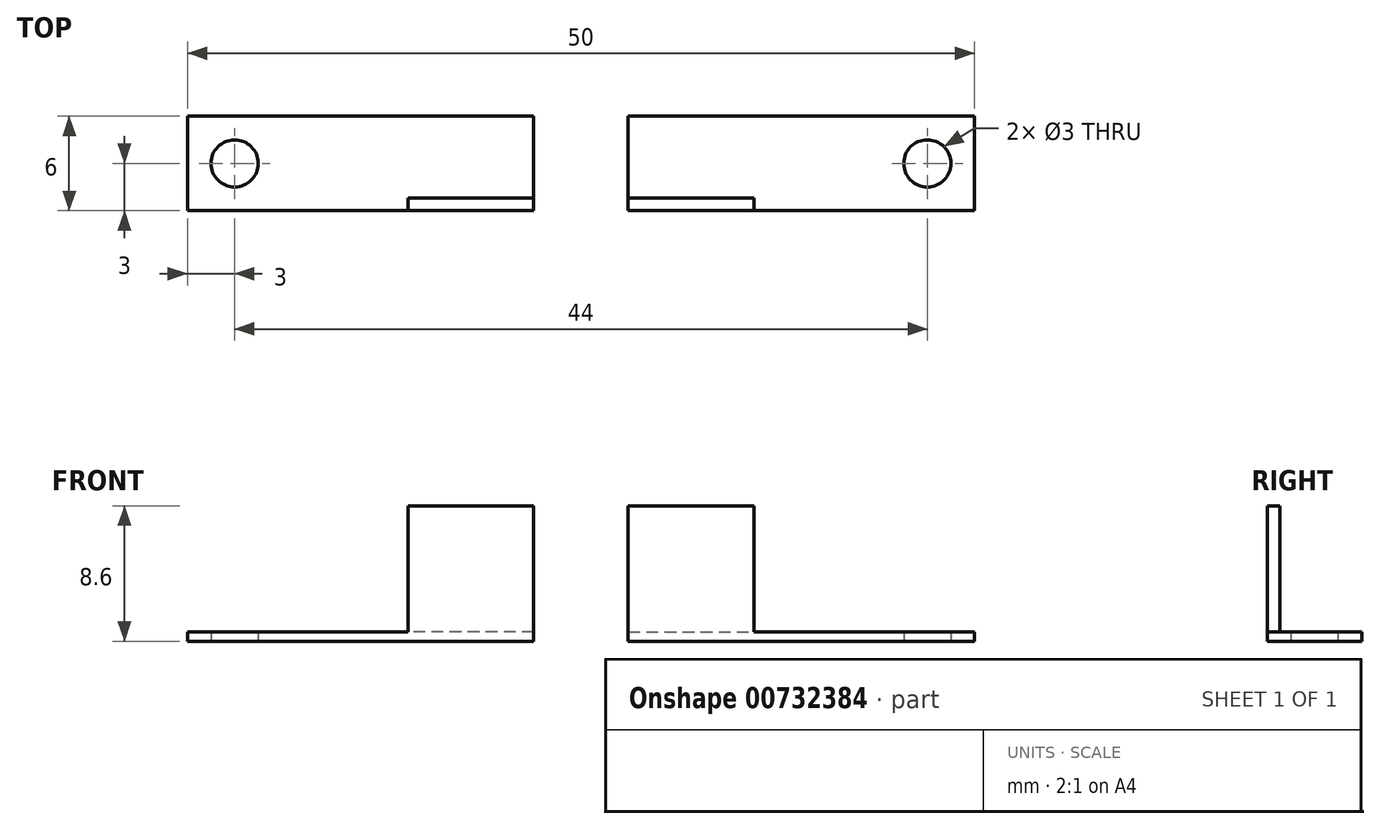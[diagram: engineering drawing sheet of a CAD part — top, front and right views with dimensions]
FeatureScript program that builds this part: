
annotation { "Feature Type Name" : "Feature", "Feature Type Description" : "" }
export const myFeature = defineFeature(function(context is Context, id is Id, definition is map)
    precondition{}
    {
        {
            var Q0;
            Q0=qCreatedBy(makeId("Top.planeOp"),FACE);
            var sketch = newSketch(context, id + "F0", { "sketchPlane" : qUnion([Q0])});
            skLineSegment(sketch, "E0.bottom", {"start": v(0, 0) * mm, "end": v(-22, 0) * mm});
            skLineSegment(sketch, "E0.top", {"start": v(0, 6) * mm, "end": v(-22, 6) * mm});
            skLineSegment(sketch, "E0.left", {"start": v(0, 0) * mm, "end": v(0, 6) * mm});
            skLineSegment(sketch, "E0.right", {"start": v(-22, 0) * mm, "end": v(-22, 6) * mm});
            skCircle(sketch, "E1", {"center": v(-3, 3) * mm, "radius": 1.5 * mm});
            skSolve(sketch);
        }
        {
            var Q0;
            Q0=makeQuery(id+"F0.imprint","IMPRINT",FACE,{"disambiguationData":[TD([[makeQuery(id+"F0.imprint","IMPRINT",EDGE,{"derivedFrom":sQuery(id+"F0.wireOp",EDGE,"E0.bottom")}),-1.0]])]});
            extrude(context, id + "F1", {"entities" : qUnion([Q0]), "depth" : 0.6 * mm, "offsetDistance" : 25 * mm});
        }
        {
            var Q0;
            Q0=makeQuery(id+"F1.opExtrude","CAP_FACE",FACE,{"disambiguationData":[OSD([sQuery(id+"F0.wireOp",EDGE,"E0.bottom"),sQuery(id+"F0.wireOp",EDGE,"E0.top"),sQuery(id+"F0.wireOp",EDGE,"E0.left"),sQuery(id+"F0.wireOp",EDGE,"E0.right"),sQuery(id+"F0.wireOp",EDGE,"E1")])],"isStart":false});
            var sketch = newSketch(context, id + "F2", { "sketchPlane" : qUnion([Q0])});
            skLineSegment(sketch, "E2.bottom", {"start": v(-22, 0) * mm, "end": v(-14, 0) * mm});
            skLineSegment(sketch, "E2.top", {"start": v(-22, 0.8) * mm, "end": v(-14, 0.8) * mm});
            skLineSegment(sketch, "E2.left", {"start": v(-22, 0) * mm, "end": v(-22, 0.8) * mm});
            skLineSegment(sketch, "E2.right", {"start": v(-14, 0) * mm, "end": v(-14, 0.8) * mm});
            skSolve(sketch);
        }
        {
            var Q0;
            Q0=makeQuery(id+"F2.imprint","IMPRINT",FACE,{"disambiguationData":[TD([[makeQuery(id+"F2.imprint","IMPRINT",EDGE,{"derivedFrom":sQuery(id+"F2.wireOp",EDGE,"E2.bottom")}),-1.0]])]});
            extrude(context, id + "F3", {"entities" : qUnion([Q0]), "operationType" : NewBodyOperationType.ADD, "depth" : 8 * mm, "offsetDistance" : 25 * mm});
        }
        {
            var Q0;
            Q0=qCreatedBy(makeId("Right.planeOp"),FACE);
            cPlane(context, id + "F4", {"entities" : qUnion([Q0]), "cplaneType" : CPlaneType.OFFSET, "offset" : 25 * mm, "oppositeDirection" : true, "width" : 150 * mm, "height" : 150 * mm});
        }
        {
            var Q0;
            Q0=makeQuery(id+"F1.opExtrude","SWEPT_BODY",BODY,{"disambiguationData":[OSD([sQuery(id+"F0.wireOp",EDGE,"E0.bottom"),sQuery(id+"F0.wireOp",EDGE,"E0.top"),sQuery(id+"F0.wireOp",EDGE,"E0.left"),sQuery(id+"F0.wireOp",EDGE,"E0.right"),sQuery(id+"F0.wireOp",EDGE,"E1")])]});
            var Q1;
            Q1=qCreatedBy(id+"F4.planeOp",FACE);
            mirror(context, id + "F5", {"entities" : qUnion([Q0]), "mirrorPlane" : qUnion([Q1])});
        }
    });
